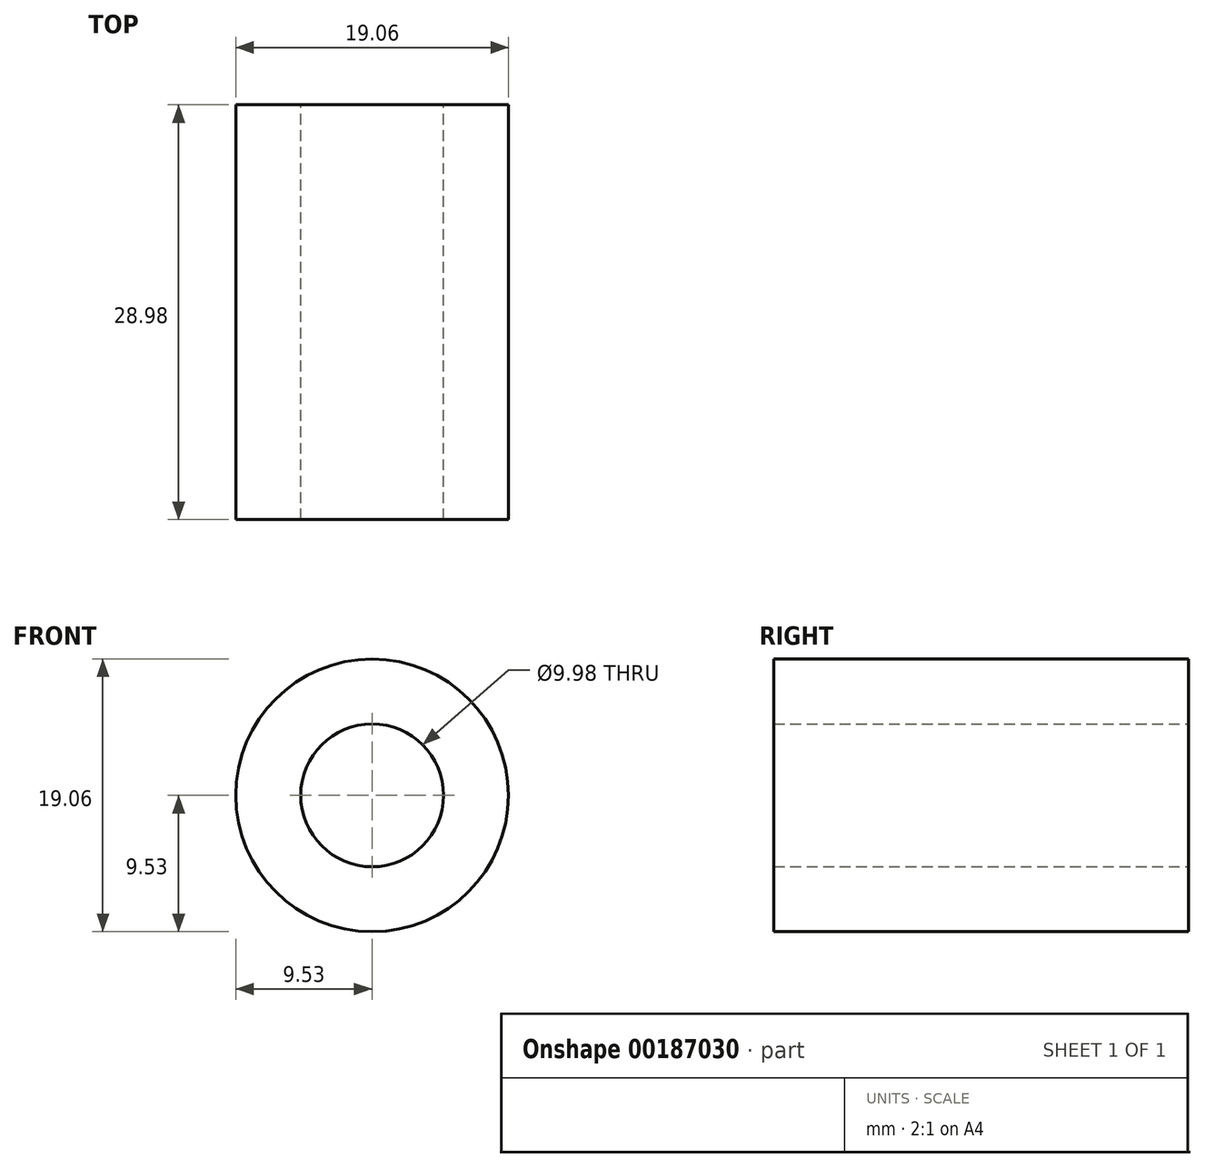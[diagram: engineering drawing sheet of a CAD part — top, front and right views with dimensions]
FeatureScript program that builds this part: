
annotation { "Feature Type Name" : "Feature", "Feature Type Description" : "" }
export const myFeature = defineFeature(function(context is Context, id is Id, definition is map)
    precondition{}
    {
        {
            var Q0;
            Q0=qCreatedBy(makeId("Front.planeOp"),FACE);
            var sketch = newSketch(context, id + "F0", { "sketchPlane" : qUnion([Q0])});
            skCircle(sketch, "E0", {"center": v(0, 0) * mm, "radius": 9.53 * mm});
            skCircle(sketch, "E1", {"center": v(0, 0) * mm, "radius": 5 * mm});
            skSolve(sketch);
        }
        {
            var Q0;
            Q0 = qSketchRegion(id + "F0", true);
            extrude(context, id + "F1", {"entities" : qUnion([Q0]), "depth" : 28.98 * mm});
        }
    });
